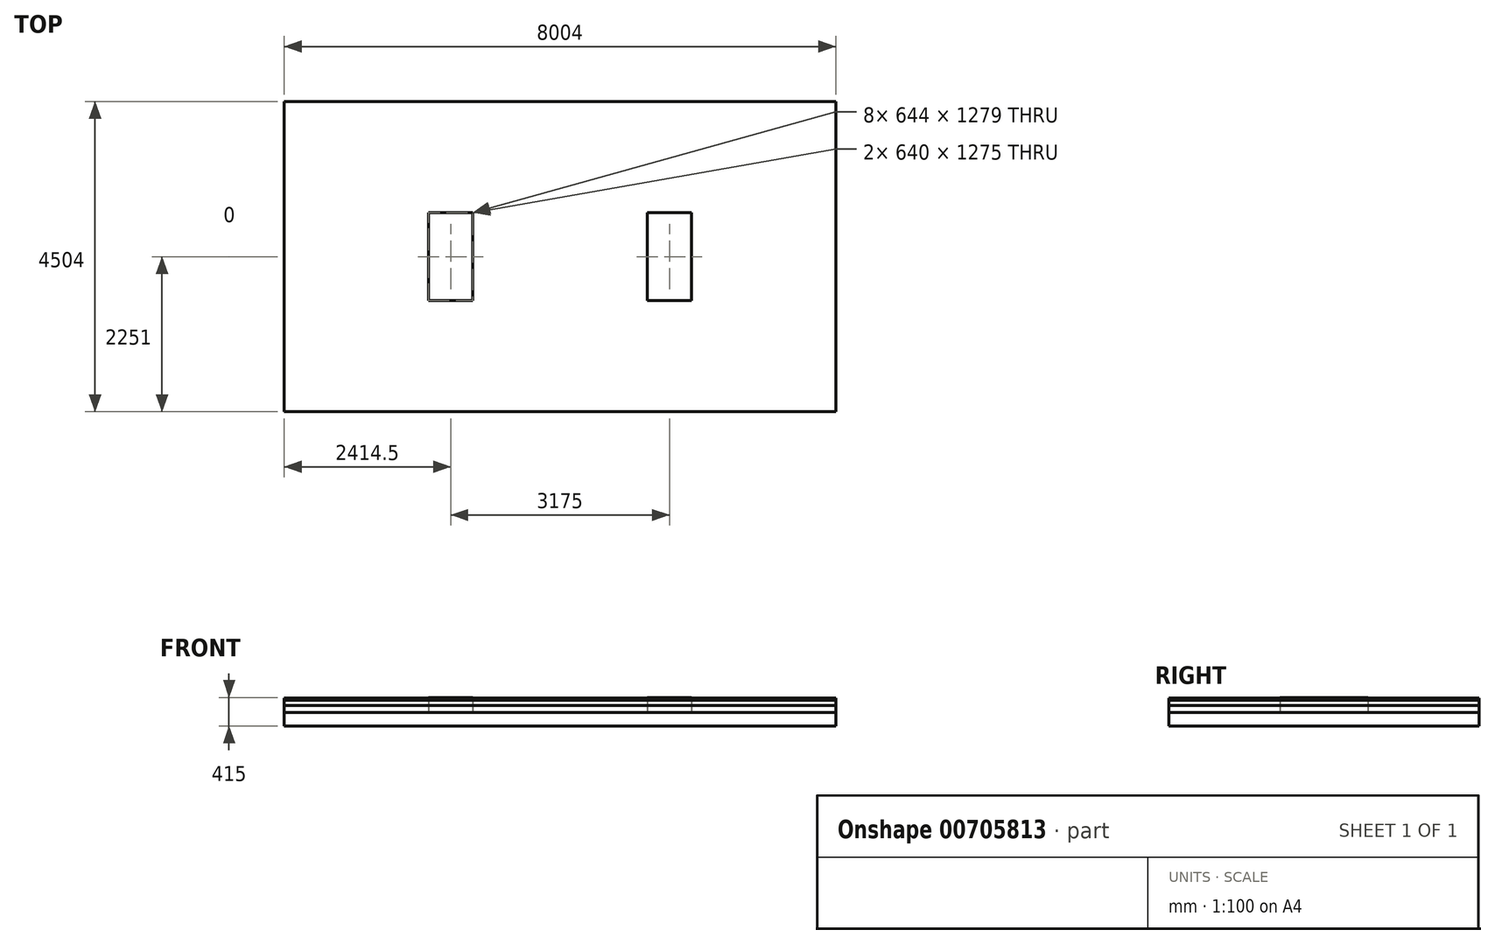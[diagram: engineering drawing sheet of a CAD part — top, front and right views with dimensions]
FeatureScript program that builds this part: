
annotation { "Feature Type Name" : "Feature", "Feature Type Description" : "" }
export const myFeature = defineFeature(function(context is Context, id is Id, definition is map)
    precondition{}
    {
        {
            var Q0;
            Q0=qCreatedBy(makeId("Top.planeOp"),FACE);
            var sketch = newSketch(context, id + "F0", { "sketchPlane" : qUnion([Q0])});
            skLineSegment(sketch, "E0.bottom", {"start": v(-113.63, -18.54) * mm, "end": v(7890.37, -18.54) * mm});
            skLineSegment(sketch, "E0.top", {"start": v(-113.63, 4485.46) * mm, "end": v(7890.37, 4485.46) * mm});
            skLineSegment(sketch, "E0.left", {"start": v(-113.63, -18.54) * mm, "end": v(-113.63, 4485.46) * mm});
            skLineSegment(sketch, "E0.right", {"start": v(7890.37, -18.54) * mm, "end": v(7890.37, 4485.46) * mm});
            skSolve(sketch);
        }
        {
            var Q0;
            Q0=makeQuery(id+"F0.imprint","IMPRINT",FACE,{"disambiguationData":[TD([[makeQuery(id+"F0.imprint","IMPRINT",EDGE,{"derivedFrom":sQuery(id+"F0.wireOp",EDGE,"E0.bottom")}),1.0]])]});
            extrude(context, id + "F1", {"entities" : qUnion([Q0]), "depth" : 200 * mm, "offsetDistance" : 25 * mm});
        }
        {
            var Q0;
            Q0=makeQuery(id+"F1.opExtrude","CAP_FACE",FACE,{"disambiguationData":[OSD([sQuery(id+"F0.wireOp",EDGE,"E0.bottom"),sQuery(id+"F0.wireOp",EDGE,"E0.top"),sQuery(id+"F0.wireOp",EDGE,"E0.left"),sQuery(id+"F0.wireOp",EDGE,"E0.right")])],"isStart":true});
            shell(context, id + "F2", {"entities" : qUnion([Q0]), "thickness" : 2 * mm});
        }
        {
            var Q0;
            Q0=makeQuery(id+"F1.opExtrude","CAP_FACE",FACE,{"disambiguationData":[OSD([sQuery(id+"F0.wireOp",EDGE,"E0.bottom"),sQuery(id+"F0.wireOp",EDGE,"E0.top"),sQuery(id+"F0.wireOp",EDGE,"E0.left"),sQuery(id+"F0.wireOp",EDGE,"E0.right")])],"isStart":false});
            var sketch = newSketch(context, id + "F3", { "sketchPlane" : qUnion([Q0])});
            skLineSegment(sketch, "E1.bottom", {"start": v(1980.87, 1594.96) * mm, "end": v(2620.87, 1594.96) * mm});
            skLineSegment(sketch, "E1.top", {"start": v(1980.87, 2869.96) * mm, "end": v(2620.87, 2869.96) * mm});
            skLineSegment(sketch, "E1.left", {"start": v(1980.87, 1594.96) * mm, "end": v(1980.87, 2869.96) * mm});
            skLineSegment(sketch, "E1.right", {"start": v(2620.87, 1594.96) * mm, "end": v(2620.87, 2869.96) * mm});
            skLineSegment(sketch, "E2.bottom", {"start": v(5155.87, 1594.96) * mm, "end": v(5795.87, 1594.96) * mm});
            skLineSegment(sketch, "E2.top", {"start": v(5155.87, 2869.96) * mm, "end": v(5795.87, 2869.96) * mm});
            skLineSegment(sketch, "E2.left", {"start": v(5155.87, 1594.96) * mm, "end": v(5155.87, 2869.96) * mm});
            skLineSegment(sketch, "E2.right", {"start": v(5795.87, 1594.96) * mm, "end": v(5795.87, 2869.96) * mm});
            skLineSegment(sketch, "E3.bottom", {"start": v(1978.87, 1592.96) * mm, "end": v(2622.87, 1592.96) * mm});
            skLineSegment(sketch, "E3.top", {"start": v(1978.87, 2871.96) * mm, "end": v(2622.87, 2871.96) * mm});
            skLineSegment(sketch, "E3.left", {"start": v(1978.87, 1592.96) * mm, "end": v(1978.87, 2871.96) * mm});
            skLineSegment(sketch, "E3.right", {"start": v(2622.87, 1592.96) * mm, "end": v(2622.87, 2871.96) * mm});
            skLineSegment(sketch, "E4.bottom", {"start": v(5153.87, 1592.96) * mm, "end": v(5797.87, 1592.96) * mm});
            skLineSegment(sketch, "E4.top", {"start": v(5153.87, 2871.96) * mm, "end": v(5797.87, 2871.96) * mm});
            skLineSegment(sketch, "E4.left", {"start": v(5153.87, 1592.96) * mm, "end": v(5153.87, 2871.96) * mm});
            skLineSegment(sketch, "E4.right", {"start": v(5797.87, 1592.96) * mm, "end": v(5797.87, 2871.96) * mm});
            skSolve(sketch);
        }
        {
            var Q0;
            Q0=makeQuery(id+"F3.imprint","IMPRINT",FACE,{"disambiguationData":[TD([[makeQuery(id+"F3.imprint","IMPRINT",EDGE,{"derivedFrom":sQuery(id+"F3.wireOp",EDGE,"E2.bottom")}),-1.0]])]});
            var Q1;
            Q1=makeQuery(id+"F3.imprint","IMPRINT",FACE,{"disambiguationData":[TD([[makeQuery(id+"F3.imprint","IMPRINT",EDGE,{"derivedFrom":sQuery(id+"F3.wireOp",EDGE,"E1.bottom")}),-1.0]])]});
            extrude(context, id + "F4", {"entities" : qUnion([Q0, Q1]), "operationType" : NewBodyOperationType.ADD, "depth" : 215 * mm, "offsetDistance" : 25 * mm});
        }
        {
            var Q0;
            Q0=makeQuery(id+"F4.boolean.opBoolean","SPLIT",FACE,{"disambiguationData":[TD([makeQuery(id+"F4.opExtrude","SWEPT_FACE",FACE,{"disambiguationData":[OSD([sQuery(id+"F3.wireOp",EDGE,"E1.bottom")])]})])],"derivedFrom":makeQuery(id+"F1.opExtrude","CAP_FACE",FACE,{"disambiguationData":[OSD([sQuery(id+"F0.wireOp",EDGE,"E0.bottom"),sQuery(id+"F0.wireOp",EDGE,"E0.top"),sQuery(id+"F0.wireOp",EDGE,"E0.left"),sQuery(id+"F0.wireOp",EDGE,"E0.right")])],"isStart":false})});
            var Q1;
            Q1=makeQuery(id+"F4.boolean.opBoolean","SPLIT",FACE,{"disambiguationData":[TD([makeQuery(id+"F4.opExtrude","SWEPT_FACE",FACE,{"disambiguationData":[OSD([sQuery(id+"F3.wireOp",EDGE,"E2.bottom")])]})])],"derivedFrom":makeQuery(id+"F1.opExtrude","CAP_FACE",FACE,{"disambiguationData":[OSD([sQuery(id+"F0.wireOp",EDGE,"E0.bottom"),sQuery(id+"F0.wireOp",EDGE,"E0.top"),sQuery(id+"F0.wireOp",EDGE,"E0.left"),sQuery(id+"F0.wireOp",EDGE,"E0.right")])],"isStart":false})});
            extrude(context, id + "F5", {"entities" : qUnion([Q0, Q1]), "operationType" : NewBodyOperationType.REMOVE, "oppositeDirection" : true, "depth" : 2 * mm, "offsetDistance" : 25 * mm});
        }
        {
            var Q0;
            {var subQ0=sQuery(id+"F0.wireOp",EDGE,"E0.right");var subQ1=sQuery(id+"F0.wireOp",EDGE,"E0.left");var subQ2=sQuery(id+"F0.wireOp",EDGE,"E0.top");var subQ3=sQuery(id+"F0.wireOp",EDGE,"E0.bottom");Q0=makeQuery(id+"F4.boolean.opBoolean","SPLIT",FACE,{"disambiguationData":[TD([makeQuery(id+"F1.opExtrude","SWEPT_FACE",FACE,{"disambiguationData":[OSD([subQ3])]})])],"derivedFrom":makeQuery(id+"F1.opExtrude","CAP_FACE",FACE,{"disambiguationData":[OSD([subQ3,subQ2,subQ1,subQ0])],"isStart":false})});}
            var sketch = newSketch(context, id + "F6", { "sketchPlane" : qUnion([Q0])});
            skLineSegment(sketch, "E5.bottom", {"start": v(-113.63, -18.54) * mm, "end": v(7890.37, -18.54) * mm});
            skLineSegment(sketch, "E5.top", {"start": v(-113.63, 4485.46) * mm, "end": v(7890.37, 4485.46) * mm});
            skLineSegment(sketch, "E5.left", {"start": v(-113.63, -18.54) * mm, "end": v(-113.63, 4485.46) * mm});
            skLineSegment(sketch, "E5.right", {"start": v(7890.37, -18.54) * mm, "end": v(7890.37, 4485.46) * mm});
            skLineSegment(sketch, "E6", {"start": v(1978.87, 1592.96) * mm, "end": v(2622.87, 1592.96) * mm});
            skLineSegment(sketch, "E7", {"start": v(2622.87, 1592.96) * mm, "end": v(2622.87, 2871.96) * mm});
            skLineSegment(sketch, "E8", {"start": v(2622.87, 2871.96) * mm, "end": v(1978.87, 2871.96) * mm});
            skLineSegment(sketch, "E9", {"start": v(1978.87, 2871.96) * mm, "end": v(1978.87, 1592.96) * mm});
            skLineSegment(sketch, "E10", {"start": v(5797.87, 2871.96) * mm, "end": v(5153.87, 2871.96) * mm});
            skLineSegment(sketch, "E11", {"start": v(5153.87, 2871.96) * mm, "end": v(5153.87, 1592.96) * mm});
            skLineSegment(sketch, "E12", {"start": v(5153.87, 1592.96) * mm, "end": v(5797.87, 1592.96) * mm});
            skLineSegment(sketch, "E13", {"start": v(5797.87, 1592.96) * mm, "end": v(5797.87, 2871.96) * mm});
            skSolve(sketch);
        }
        {
            var Q0;
            Q0=makeQuery(id+"F6.imprint","IMPRINT",FACE,{"disambiguationData":[TD([[makeQuery(id+"F6.imprint","IMPRINT",EDGE,{"derivedFrom":sQuery(id+"F6.wireOp",EDGE,"E5.bottom")}),1.0]])]});
            extrude(context, id + "F7", {"entities" : qUnion([Q0]), "depth" : 100 * mm, "offsetDistance" : 25 * mm});
        }
        {
            var Q0;
            Q0=makeQuery(id+"F7.opExtrude","CAP_FACE",FACE,{"disambiguationData":[OSD([sQuery(id+"F6.wireOp",EDGE,"E5.bottom"),sQuery(id+"F6.wireOp",EDGE,"E5.top"),sQuery(id+"F6.wireOp",EDGE,"E5.left"),sQuery(id+"F6.wireOp",EDGE,"E5.right"),sQuery(id+"F6.wireOp",EDGE,"E6"),sQuery(id+"F6.wireOp",EDGE,"E7"),sQuery(id+"F6.wireOp",EDGE,"E8"),sQuery(id+"F6.wireOp",EDGE,"E9"),sQuery(id+"F6.wireOp",EDGE,"E10"),sQuery(id+"F6.wireOp",EDGE,"E11"),sQuery(id+"F6.wireOp",EDGE,"E12"),sQuery(id+"F6.wireOp",EDGE,"E13")])],"isStart":false});
            extrude(context, id + "F8", {"entities" : qUnion([Q0]), "depth" : 75 * mm, "offsetDistance" : 25 * mm});
        }
        {
            var Q0;
            Q0=makeQuery(id+"F8.opExtrude","CAP_FACE",FACE,{"disambiguationData":[OSD([sQuery(id+"F6.wireOp",EDGE,"E5.bottom"),sQuery(id+"F6.wireOp",EDGE,"E5.top"),sQuery(id+"F6.wireOp",EDGE,"E5.left"),sQuery(id+"F6.wireOp",EDGE,"E5.right"),sQuery(id+"F6.wireOp",EDGE,"E6"),sQuery(id+"F6.wireOp",EDGE,"E7"),sQuery(id+"F6.wireOp",EDGE,"E8"),sQuery(id+"F6.wireOp",EDGE,"E9"),sQuery(id+"F6.wireOp",EDGE,"E10"),sQuery(id+"F6.wireOp",EDGE,"E11"),sQuery(id+"F6.wireOp",EDGE,"E12"),sQuery(id+"F6.wireOp",EDGE,"E13")])],"isStart":false});
            extrude(context, id + "F9", {"entities" : qUnion([Q0]), "depth" : 7 * mm, "offsetDistance" : 25 * mm});
        }
        {
            var Q0;
            Q0=makeQuery(id+"F9.opExtrude","CAP_FACE",FACE,{"disambiguationData":[OSD([sQuery(id+"F6.wireOp",EDGE,"E5.bottom"),sQuery(id+"F6.wireOp",EDGE,"E5.top"),sQuery(id+"F6.wireOp",EDGE,"E5.left"),sQuery(id+"F6.wireOp",EDGE,"E5.right"),sQuery(id+"F6.wireOp",EDGE,"E6"),sQuery(id+"F6.wireOp",EDGE,"E7"),sQuery(id+"F6.wireOp",EDGE,"E8"),sQuery(id+"F6.wireOp",EDGE,"E9"),sQuery(id+"F6.wireOp",EDGE,"E10"),sQuery(id+"F6.wireOp",EDGE,"E11"),sQuery(id+"F6.wireOp",EDGE,"E12"),sQuery(id+"F6.wireOp",EDGE,"E13")])],"isStart":false});
            extrude(context, id + "F10", {"entities" : qUnion([Q0]), "depth" : 25 * mm, "offsetDistance" : 25 * mm});
        }
    });
